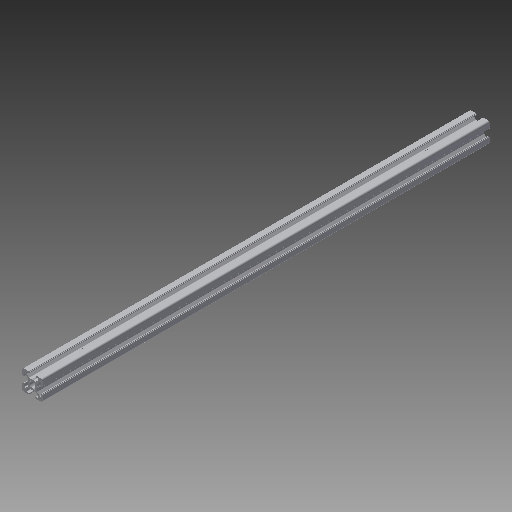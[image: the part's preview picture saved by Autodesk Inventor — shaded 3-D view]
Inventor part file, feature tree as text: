
AUTODESK INVENTOR PART (.ipt)
format: ipt  version: 2017 (Build 210142000, 142)  size: 403,968 bytes
history: native  units: in
note: dims shown in document units (in); Inventor stores cm internally (conversion verified against a paired STEP export)
features: other x3, sketch x2, extrude x1, hole x1, mirror x1
ambient origin geometry x8: Origin, YZ Plane, XZ Plane, XY Plane, X Axis, Y Axis, Z Axis, Center Point
bodies: Solid1 (feature_tree)
feature tree (8):
  other  "Blocks"
  extrude  "Extrusion1"  Depth=2.0in
  hole  "Hole1"  [1 undecoded]
  mirror  "Mirror1"
  sketch  "Sketch1"  dims[d1=0.0in d5=2.0in]
  other  "20x20"
  sketch  "Sketch3"  dims[d6=0.187in d7=0.75in d8=0.375in d9=0.25in d10=0.5635in d11=1.0in d12=0.8108in d13=1.0in d14=1.0in]
  other  "20x20:1"
note: 1 required parameter value undecoded (feature->parameter linkage not recoverable at this tier; creation-order binding heuristic only, values carry confidence <= 0.55)
